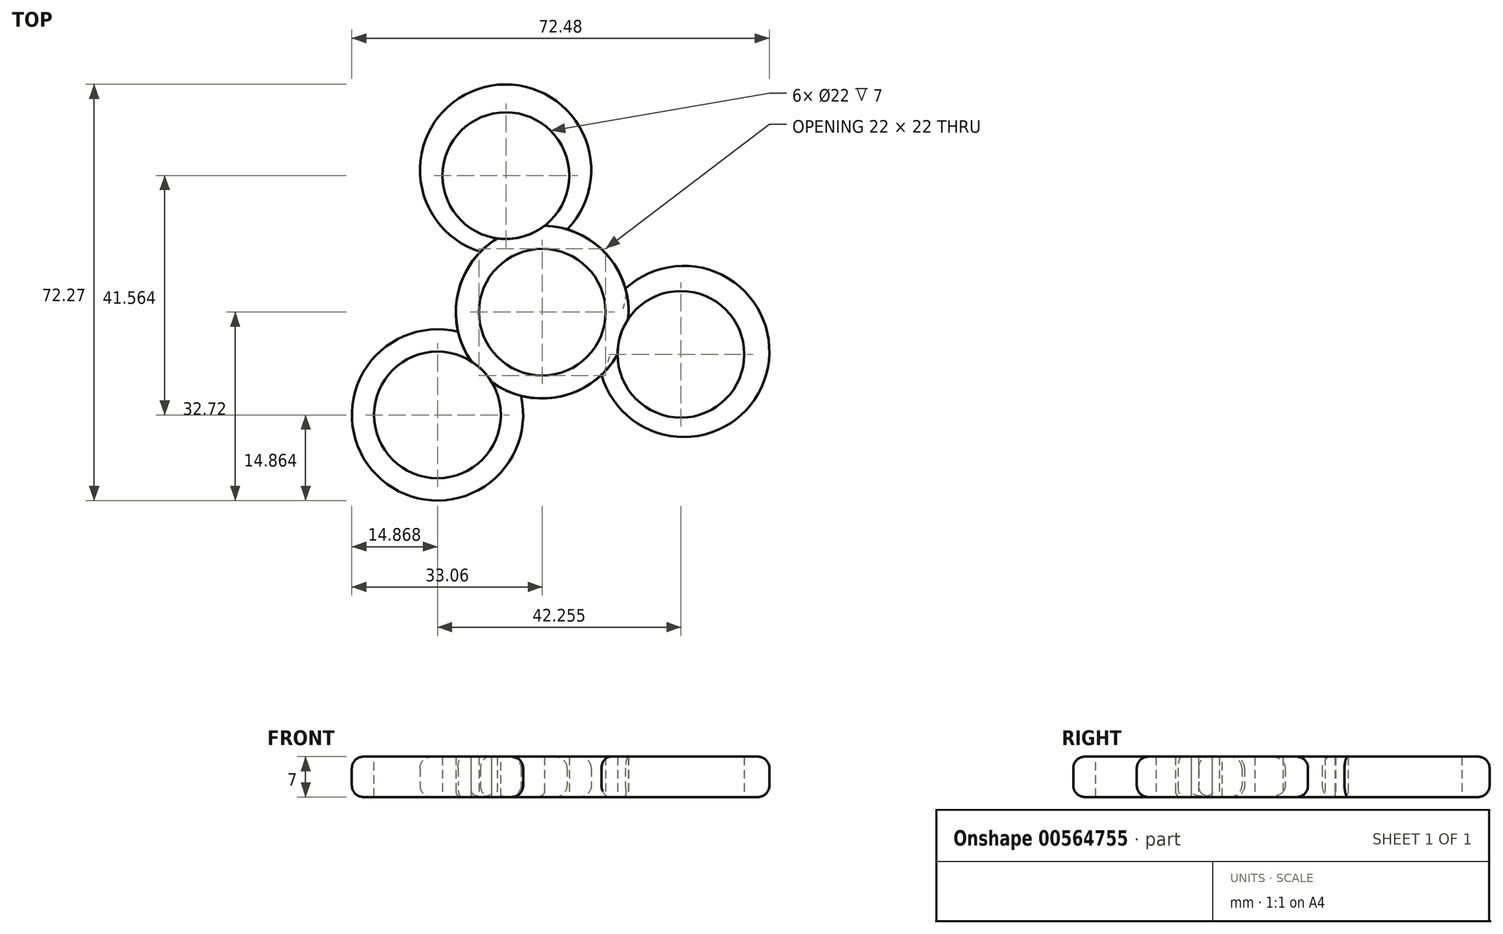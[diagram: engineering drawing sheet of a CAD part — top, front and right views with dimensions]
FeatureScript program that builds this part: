
annotation { "Feature Type Name" : "Feature", "Feature Type Description" : "" }
export const myFeature = defineFeature(function(context is Context, id is Id, definition is map)
    precondition{}
    {
        {
            var Q0;
            Q0=qCreatedBy(makeId("Top.planeOp"),FACE);
            var sketch = newSketch(context, id + "F0", { "sketchPlane" : qUnion([Q0])});
            skCircle(sketch, "E0", {"center": v(0, 0) * mm, "radius": 15 * mm});
            skSolve(sketch);
        }
        {
            var Q0;
            Q0=qCreatedBy(makeId("Top.planeOp"),FACE);
            var sketch = newSketch(context, id + "F1", { "sketchPlane" : qUnion([Q0])});
            skCircle(sketch, "E1", {"center": v(-18.2, -17.86) * mm, "radius": 14.86 * mm});
            skCircle(sketch, "E2", {"center": v(-13.73, -17.84) * mm, "radius": 2.94 * mm});
            skSolve(sketch);
        }
        {
            var Q0;
            Q0=makeQuery(id+"F1.imprint","IMPRINT",FACE,{"disambiguationData":[TD([[makeQuery(id+"F1.imprint","IMPRINT",EDGE,{"derivedFrom":sQuery(id+"F1.wireOp",EDGE,"E1")}),1.0]])]});
            extrude(context, id + "F2", {"entities" : qUnion([Q0]), "depth" : 7 * mm, "offsetDistance" : 25 * mm});
        }
        {
            var Q0;
            Q0=makeQuery(id+"F1.imprint","IMPRINT",FACE,{"disambiguationData":[TD([[makeQuery(id+"F1.imprint","IMPRINT",EDGE,{"derivedFrom":sQuery(id+"F1.wireOp",EDGE,"E2")}),1.0]])]});
            extrude(context, id + "F3", {"entities" : qUnion([Q0]), "operationType" : NewBodyOperationType.ADD, "depth" : 7 * mm, "offsetDistance" : 25 * mm});
        }
        {
            var Q0;
            Q0=makeQuery(id+"F0.imprint","IMPRINT",FACE,{"disambiguationData":[TD([[makeQuery(id+"F0.imprint","IMPRINT",EDGE,{"derivedFrom":sQuery(id+"F0.wireOp",EDGE,"E0")}),1.0]])]});
            extrude(context, id + "F4", {"entities" : qUnion([Q0]), "operationType" : NewBodyOperationType.ADD, "depth" : 7 * mm, "offsetDistance" : 25 * mm});
        }
        {
            var Q0;
            Q0=makeQuery(id+"F2.opExtrude","SWEPT_BODY",BODY,{"disambiguationData":[OSD([sQuery(id+"F1.wireOp",EDGE,"E1"),sQuery(id+"F1.wireOp",EDGE,"E2")])]});
            var Q1;
            Q1=makeQuery(id+"F4.opExtrude","SWEPT_FACE",FACE,{"disambiguationData":[OSD([sQuery(id+"F0.wireOp",EDGE,"E0")])]});
            circularPattern(context, id + "F5", {"entities" : qUnion([Q0]), "axis" : qUnion([Q1]), "angle" : 360 * degree, "instanceCount" : 3, "equalSpace" : true});
        }
        {
            var Q0;
            Q0=qCreatedBy(makeId("Top.planeOp"),FACE);
            var sketch = newSketch(context, id + "F6", { "sketchPlane" : qUnion([Q0])});
            skCircle(sketch, "E3", {"center": v(0, 0) * mm, "radius": 9.8 * mm});
            skSolve(sketch);
        }
        {
            var Q0;
            Q0=sQuery(id+"F6.wireOp",VERTEX,"E3.center");
            var Q1;
            Q1=makeQuery(id+"F2.opExtrude","SWEPT_BODY",BODY,{"disambiguationData":[OSD([sQuery(id+"F1.wireOp",EDGE,"E1"),sQuery(id+"F1.wireOp",EDGE,"E2")])]});
            var Q2;
            Q2=makeQuery(id+"F5.opPattern","COPY",BODY,{"derivedFrom":makeQuery(id+"F2.opExtrude","SWEPT_BODY",BODY,{"disambiguationData":[OSD([sQuery(id+"F1.wireOp",EDGE,"E1"),sQuery(id+"F1.wireOp",EDGE,"E2")])]}),"instanceName":"1"});
            var Q3;
            Q3=makeQuery(id+"F5.opPattern","COPY",BODY,{"derivedFrom":makeQuery(id+"F2.opExtrude","SWEPT_BODY",BODY,{"disambiguationData":[OSD([sQuery(id+"F1.wireOp",EDGE,"E1"),sQuery(id+"F1.wireOp",EDGE,"E2")])]}),"instanceName":"2"});
            hole(context, id + "F7", {"style" : HoleStyle.SIMPLE, "endStyle" : HoleEndStyle.THROUGH, "oppositeDirection" : true, "holeDiameter" : 22 * mm, "majorDiameter" : 5 * mm, "isTappedThrough" : true, "tappedDepth" : 12 * mm, "tapClearance" : 3, "locations" : qUnion([Q0]), "scope" : qUnion([Q1, Q2, Q3])});
        }
        {
            var Q0;
            {var subQ0=sQuery(id+"F1.wireOp",EDGE,"E2");Q0=makeQuery(id+"F4.boolean.opBoolean","MERGE",FACE,{"derivedFrom":[makeQuery(id+"F3.boolean.opBoolean","MERGE",FACE,{"derivedFrom":[makeQuery(id+"F2.opExtrude","CAP_FACE",FACE,{"disambiguationData":[OSD([sQuery(id+"F1.wireOp",EDGE,"E1"),subQ0])],"isStart":false}),makeQuery(id+"F3.opExtrude","CAP_FACE",FACE,{"disambiguationData":[OSD([subQ0])],"isStart":false})]}),makeQuery(id+"F4.opExtrude","CAP_FACE",FACE,{"disambiguationData":[OSD([sQuery(id+"F0.wireOp",EDGE,"E0")])],"isStart":false})]});}
            var sketch = newSketch(context, id + "F8", { "sketchPlane" : qUnion([Q0])});
            skCircle(sketch, "E4", {"center": v(-18.2, -17.86) * mm, "radius": 11.77 * mm});
            skSolve(sketch);
        }
        {
            var Q0;
            Q0=sQuery(id+"F8.wireOp",VERTEX,"E4.center");
            var Q1;
            Q1=makeQuery(id+"F2.opExtrude","SWEPT_BODY",BODY,{"disambiguationData":[OSD([sQuery(id+"F1.wireOp",EDGE,"E1"),sQuery(id+"F1.wireOp",EDGE,"E2")])]});
            var Q2;
            Q2=makeQuery(id+"F5.opPattern","COPY",BODY,{"derivedFrom":makeQuery(id+"F2.opExtrude","SWEPT_BODY",BODY,{"disambiguationData":[OSD([sQuery(id+"F1.wireOp",EDGE,"E1"),sQuery(id+"F1.wireOp",EDGE,"E2")])]}),"instanceName":"1"});
            var Q3;
            Q3=makeQuery(id+"F5.opPattern","COPY",BODY,{"derivedFrom":makeQuery(id+"F2.opExtrude","SWEPT_BODY",BODY,{"disambiguationData":[OSD([sQuery(id+"F1.wireOp",EDGE,"E1"),sQuery(id+"F1.wireOp",EDGE,"E2")])]}),"instanceName":"2"});
            hole(context, id + "F9", {"style" : HoleStyle.SIMPLE, "endStyle" : HoleEndStyle.THROUGH, "holeDiameter" : 22 * mm, "majorDiameter" : 5 * mm, "isTappedThrough" : true, "tappedDepth" : 12 * mm, "tapClearance" : 3, "locations" : qUnion([Q0]), "scope" : qUnion([Q1, Q2, Q3])});
        }
        {
            var Q0;
            Q0=qCreatedBy(makeId("Top.planeOp"),FACE);
            var sketch = newSketch(context, id + "F10", { "sketchPlane" : qUnion([Q0])});
            skCircle(sketch, "E5", {"center": v(-6.31, 23.7) * mm, "radius": 10.56 * mm});
            skSolve(sketch);
        }
        {
            var Q0;
            Q0=sQuery(id+"F10.wireOp",VERTEX,"E5.center");
            var Q1;
            Q1=makeQuery(id+"F2.opExtrude","SWEPT_BODY",BODY,{"disambiguationData":[OSD([sQuery(id+"F1.wireOp",EDGE,"E1"),sQuery(id+"F1.wireOp",EDGE,"E2")])]});
            var Q2;
            Q2=makeQuery(id+"F5.opPattern","COPY",BODY,{"derivedFrom":makeQuery(id+"F2.opExtrude","SWEPT_BODY",BODY,{"disambiguationData":[OSD([sQuery(id+"F1.wireOp",EDGE,"E1"),sQuery(id+"F1.wireOp",EDGE,"E2")])]}),"instanceName":"1"});
            var Q3;
            Q3=makeQuery(id+"F5.opPattern","COPY",BODY,{"derivedFrom":makeQuery(id+"F2.opExtrude","SWEPT_BODY",BODY,{"disambiguationData":[OSD([sQuery(id+"F1.wireOp",EDGE,"E1"),sQuery(id+"F1.wireOp",EDGE,"E2")])]}),"instanceName":"2"});
            hole(context, id + "F11", {"style" : HoleStyle.SIMPLE, "endStyle" : HoleEndStyle.THROUGH, "oppositeDirection" : true, "holeDiameter" : 22 * mm, "majorDiameter" : 5 * mm, "isTappedThrough" : true, "tappedDepth" : 12 * mm, "tapClearance" : 3, "locations" : qUnion([Q0]), "scope" : qUnion([Q1, Q2, Q3])});
        }
        {
            var Q0;
            Q0=qCreatedBy(makeId("Top.planeOp"),FACE);
            var sketch = newSketch(context, id + "F12", { "sketchPlane" : qUnion([Q0])});
            skCircle(sketch, "E6", {"center": v(24.06, -7.34) * mm, "radius": 10.5 * mm});
            skSolve(sketch);
        }
        {
            var Q0;
            Q0=sQuery(id+"F12.wireOp",VERTEX,"E6.center");
            var Q1;
            Q1=makeQuery(id+"F2.opExtrude","SWEPT_BODY",BODY,{"disambiguationData":[OSD([sQuery(id+"F1.wireOp",EDGE,"E1"),sQuery(id+"F1.wireOp",EDGE,"E2")])]});
            var Q2;
            Q2=makeQuery(id+"F5.opPattern","COPY",BODY,{"derivedFrom":makeQuery(id+"F2.opExtrude","SWEPT_BODY",BODY,{"disambiguationData":[OSD([sQuery(id+"F1.wireOp",EDGE,"E1"),sQuery(id+"F1.wireOp",EDGE,"E2")])]}),"instanceName":"1"});
            var Q3;
            Q3=makeQuery(id+"F5.opPattern","COPY",BODY,{"derivedFrom":makeQuery(id+"F2.opExtrude","SWEPT_BODY",BODY,{"disambiguationData":[OSD([sQuery(id+"F1.wireOp",EDGE,"E1"),sQuery(id+"F1.wireOp",EDGE,"E2")])]}),"instanceName":"2"});
            hole(context, id + "F13", {"style" : HoleStyle.SIMPLE, "endStyle" : HoleEndStyle.THROUGH, "oppositeDirection" : true, "holeDiameter" : 22 * mm, "majorDiameter" : 5 * mm, "isTappedThrough" : true, "tappedDepth" : 12 * mm, "tapClearance" : 3, "locations" : qUnion([Q0]), "scope" : qUnion([Q1, Q2, Q3])});
        }
        {
            var Q0;
            Q0=makeQuery(id+"F5.opPattern","COPY",EDGE,{"derivedFrom":makeQuery(id+"F2.opExtrude","CAP_EDGE",EDGE,{"disambiguationData":[OSD([sQuery(id+"F1.wireOp",EDGE,"E1")])],"isStart":false}),"instanceName":"1"});
            fillet(context, id + "F14", {"entities" : qUnion([Q0]), "radius" : 2 * mm, "tangentPropagation" : true, "allowEdgeOverflow" : false});
        }
        {
            var Q0;
            Q0=makeQuery(id+"F5.opPattern","COPY",EDGE,{"derivedFrom":makeQuery(id+"F2.opExtrude","CAP_EDGE",EDGE,{"disambiguationData":[OSD([sQuery(id+"F1.wireOp",EDGE,"E1")])],"isStart":true}),"instanceName":"1"});
            fillet(context, id + "F15", {"entities" : qUnion([Q0]), "radius" : 2 * mm, "tangentPropagation" : true, "allowEdgeOverflow" : false});
        }
        {
            var Q0;
            Q0=makeQuery(id+"F5.opPattern","COPY",EDGE,{"derivedFrom":makeQuery(id+"F2.opExtrude","CAP_EDGE",EDGE,{"disambiguationData":[OSD([sQuery(id+"F1.wireOp",EDGE,"E1")])],"isStart":true}),"instanceName":"2"});
            fillet(context, id + "F16", {"entities" : qUnion([Q0]), "radius" : 2 * mm, "tangentPropagation" : true, "allowEdgeOverflow" : false});
        }
        {
            var Q0;
            Q0=makeQuery(id+"F5.opPattern","COPY",EDGE,{"derivedFrom":makeQuery(id+"F2.opExtrude","CAP_EDGE",EDGE,{"disambiguationData":[OSD([sQuery(id+"F1.wireOp",EDGE,"E1")])],"isStart":false}),"instanceName":"2"});
            fillet(context, id + "F17", {"entities" : qUnion([Q0]), "radius" : 2 * mm, "tangentPropagation" : true, "allowEdgeOverflow" : false});
        }
        {
            var Q0;
            Q0=makeQuery(id+"F2.opExtrude","CAP_EDGE",EDGE,{"disambiguationData":[OSD([sQuery(id+"F1.wireOp",EDGE,"E1")])],"isStart":false});
            fillet(context, id + "F18", {"entities" : qUnion([Q0]), "radius" : 2 * mm, "tangentPropagation" : true, "allowEdgeOverflow" : false});
        }
        {
            var Q0;
            Q0=makeQuery(id+"F2.opExtrude","CAP_EDGE",EDGE,{"disambiguationData":[OSD([sQuery(id+"F1.wireOp",EDGE,"E1")])],"isStart":true});
            fillet(context, id + "F19", {"entities" : qUnion([Q0]), "radius" : 2 * mm, "tangentPropagation" : true, "allowEdgeOverflow" : false});
        }
        {
            var Q0;
            {var subQ0=sQuery(id+"F0.wireOp",EDGE,"E0");var subQ2=sQuery(id+"F1.wireOp",EDGE,"E1");Q0=makeQuery(id+"F11.hole-0.boolean.opBoolean","SPLIT",EDGE,{"disambiguationData":[TD([makeQuery(id+"F5.opPattern","COPY",FACE,{"derivedFrom":makeQuery(id+"F2.opExtrude","SWEPT_FACE",FACE,{"disambiguationData":[OSD([subQ2])]}),"instanceName":"2"})])],"derivedFrom":makeQuery(id+"F9.hole-0.boolean.opBoolean","SPLIT",EDGE,{"disambiguationData":[OD(1.0)],"derivedFrom":makeQuery(id+"F5.opPattern","COPY",EDGE,{"derivedFrom":makeQuery(id+"F4.opExtrude","CAP_EDGE",EDGE,{"disambiguationData":[OSD([subQ0])],"isStart":true}),"instanceName":"2"})})});}
            fillet(context, id + "F20", {"entities" : qUnion([Q0]), "radius" : 1 * mm, "tangentPropagation" : true, "allowEdgeOverflow" : false});
        }
    });
